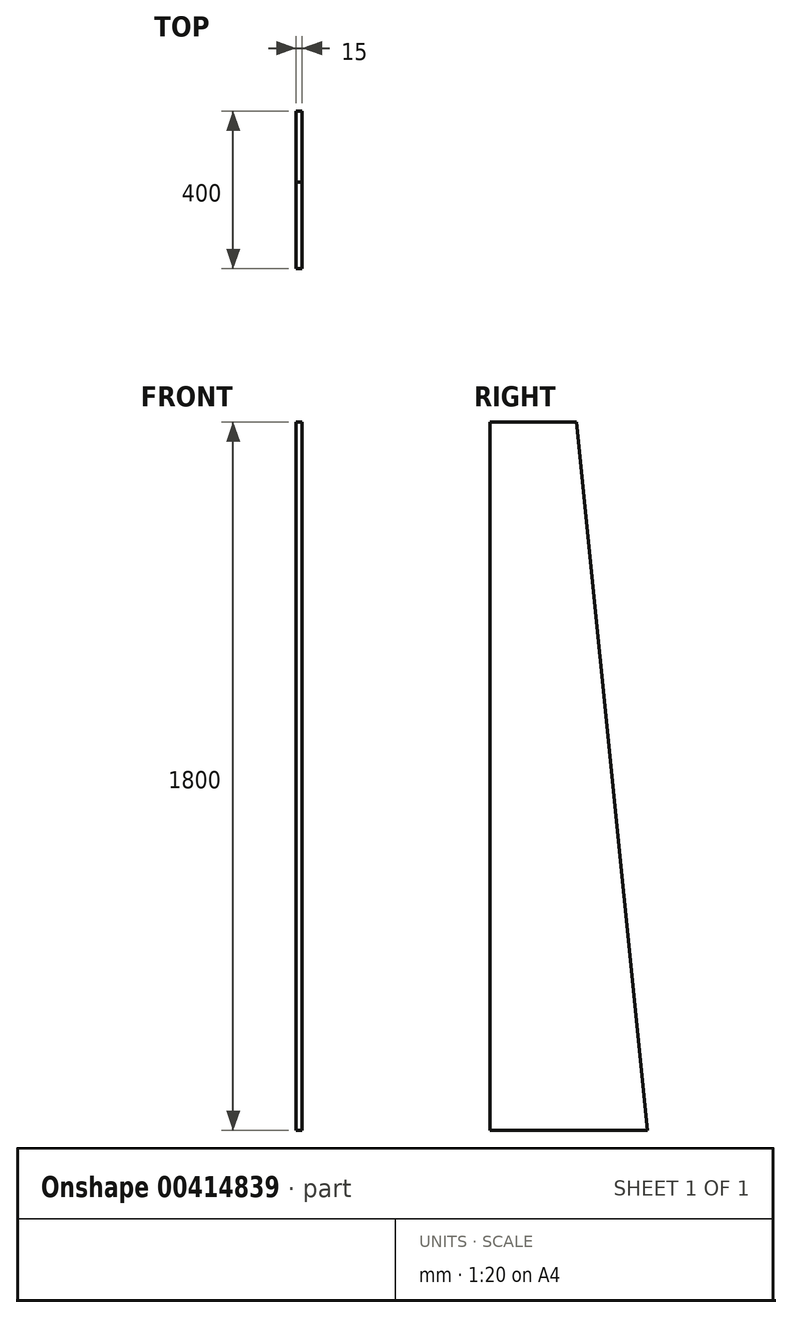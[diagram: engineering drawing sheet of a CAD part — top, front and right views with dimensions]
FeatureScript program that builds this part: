
annotation { "Feature Type Name" : "Feature", "Feature Type Description" : "" }
export const myFeature = defineFeature(function(context is Context, id is Id, definition is map)
    precondition{}
    {
        {
            var Q0;
            Q0=qCreatedBy(makeId("Right.planeOp"),FACE);
            var sketch = newSketch(context, id + "F0", { "sketchPlane" : qUnion([Q0])});
            skLineSegment(sketch, "E0", {"start": v(0, 0) * mm, "end": v(0, 1800) * mm});
            skLineSegment(sketch, "E1", {"start": v(0, 1800) * mm, "end": v(220, 1800) * mm});
            skLineSegment(sketch, "E2", {"start": v(220, 1800) * mm, "end": v(400, 0) * mm});
            skLineSegment(sketch, "E3", {"start": v(400, 0) * mm, "end": v(0, 0) * mm});
            skSolve(sketch);
        }
        {
            var Q0;
            Q0 = qSketchRegion(id + "F0", true);
            extrude(context, id + "F1", {"entities" : qUnion([Q0]), "depth" : 15 * mm});
        }
    });
